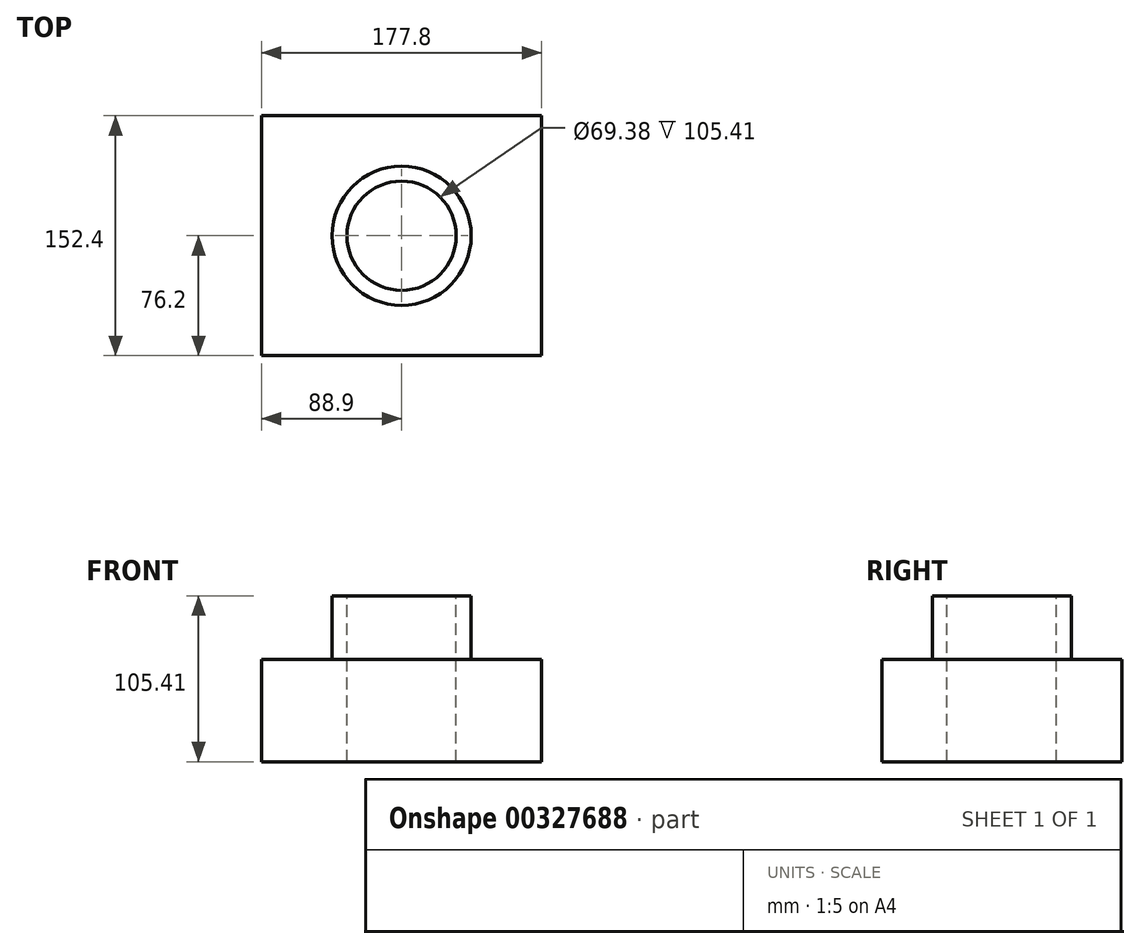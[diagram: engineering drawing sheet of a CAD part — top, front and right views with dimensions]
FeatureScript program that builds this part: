
annotation { "Feature Type Name" : "Feature", "Feature Type Description" : "" }
export const myFeature = defineFeature(function(context is Context, id is Id, definition is map)
    precondition{}
    {
        {
            var Q0;
            Q0=qCreatedBy(makeId("Top.planeOp"),FACE);
            var sketch = newSketch(context, id + "F0", { "sketchPlane" : qUnion([Q0])});
            skLineSegment(sketch, "E0.bottom", {"start": v(76.2, 76.2) * mm, "end": v(-76.2, 76.2) * mm});
            skLineSegment(sketch, "E0.top", {"start": v(76.2, -76.2) * mm, "end": v(-76.2, -76.2) * mm});
            skLineSegment(sketch, "E0.left", {"start": v(76.2, 76.2) * mm, "end": v(76.2, -76.2) * mm});
            skLineSegment(sketch, "E0.right", {"start": v(-76.2, 76.2) * mm, "end": v(-76.2, -76.2) * mm});
            skPoint(sketch, "E0.middle", {"position": v(0, 0) * mm});
            skSolve(sketch);
        }
        {
            var Q0;
            Q0=makeQuery(id+"F0.imprint","IMPRINT",FACE,{"disambiguationData":[TD([[makeQuery(id+"F0.imprint","IMPRINT",EDGE,{"derivedFrom":sQuery(id+"F0.wireOp",EDGE,"E0.bottom")}),1.0]])]});
            extrude(context, id + "F1", {"entities" : qUnion([Q0]), "depth" : 65.02 * mm});
        }
        {
            var Q0;
            Q0=makeQuery(id+"F1.opExtrude","CAP_FACE",FACE,{"disambiguationData":[OSD([sQuery(id+"F0.wireOp",EDGE,"E0.bottom"),sQuery(id+"F0.wireOp",EDGE,"E0.top"),sQuery(id+"F0.wireOp",EDGE,"E0.left"),sQuery(id+"F0.wireOp",EDGE,"E0.right")])],"isStart":false});
            var sketch = newSketch(context, id + "F2", { "sketchPlane" : qUnion([Q0])});
            skCircle(sketch, "E1", {"center": v(0, 0) * mm, "radius": 44.97 * mm});
            skCircle(sketch, "E2", {"center": v(0, 0) * mm, "radius": 34.7 * mm});
            skSolve(sketch);
        }
        {
            var Q0;
            Q0=makeQuery(id+"F2.imprint","IMPRINT",FACE,{"disambiguationData":[TD([[makeQuery(id+"F2.imprint","IMPRINT",EDGE,{"derivedFrom":sQuery(id+"F2.wireOp",EDGE,"E2")}),1.0]])]});
            extrude(context, id + "F3", {"entities" : qUnion([Q0]), "operationType" : NewBodyOperationType.REMOVE, "oppositeDirection" : true, "depth" : 125.98 * mm});
        }
        {
            var Q0;
            Q0=makeQuery(id+"F1.opExtrude","CAP_FACE",FACE,{"disambiguationData":[OSD([sQuery(id+"F0.wireOp",EDGE,"E0.bottom"),sQuery(id+"F0.wireOp",EDGE,"E0.top"),sQuery(id+"F0.wireOp",EDGE,"E0.left"),sQuery(id+"F0.wireOp",EDGE,"E0.right")])],"isStart":false});
            var sketch = newSketch(context, id + "F4", { "sketchPlane" : qUnion([Q0])});
            skCircle(sketch, "E3", {"center": v(0, 0) * mm, "radius": 44.19 * mm});
            skSolve(sketch);
        }
        {
            var Q0;
            Q0=makeQuery(id+"F4.imprint","IMPRINT",FACE,{"disambiguationData":[TD([[makeQuery(id+"F4.imprint","IMPRINT",EDGE,{"derivedFrom":sQuery(id+"F4.wireOp",EDGE,"E3")}),1.0]])]});
            extrude(context, id + "F5", {"entities" : qUnion([Q0]), "operationType" : NewBodyOperationType.ADD, "depth" : 40.4 * mm});
        }
        {
            var Q0;
            Q0=makeQuery(id+"F1.opExtrude","SWEPT_FACE",FACE,{"disambiguationData":[OSD([sQuery(id+"F0.wireOp",EDGE,"E0.left")])]});
            extrude(context, id + "F6", {"entities" : qUnion([Q0]), "operationType" : NewBodyOperationType.ADD, "depth" : 12.7 * mm});
        }
        {
            var Q0;
            Q0=makeQuery(id+"F1.opExtrude","SWEPT_FACE",FACE,{"disambiguationData":[OSD([sQuery(id+"F0.wireOp",EDGE,"E0.right")])]});
            extrude(context, id + "F7", {"entities" : qUnion([Q0]), "operationType" : NewBodyOperationType.ADD, "depth" : 12.7 * mm});
        }
    });
